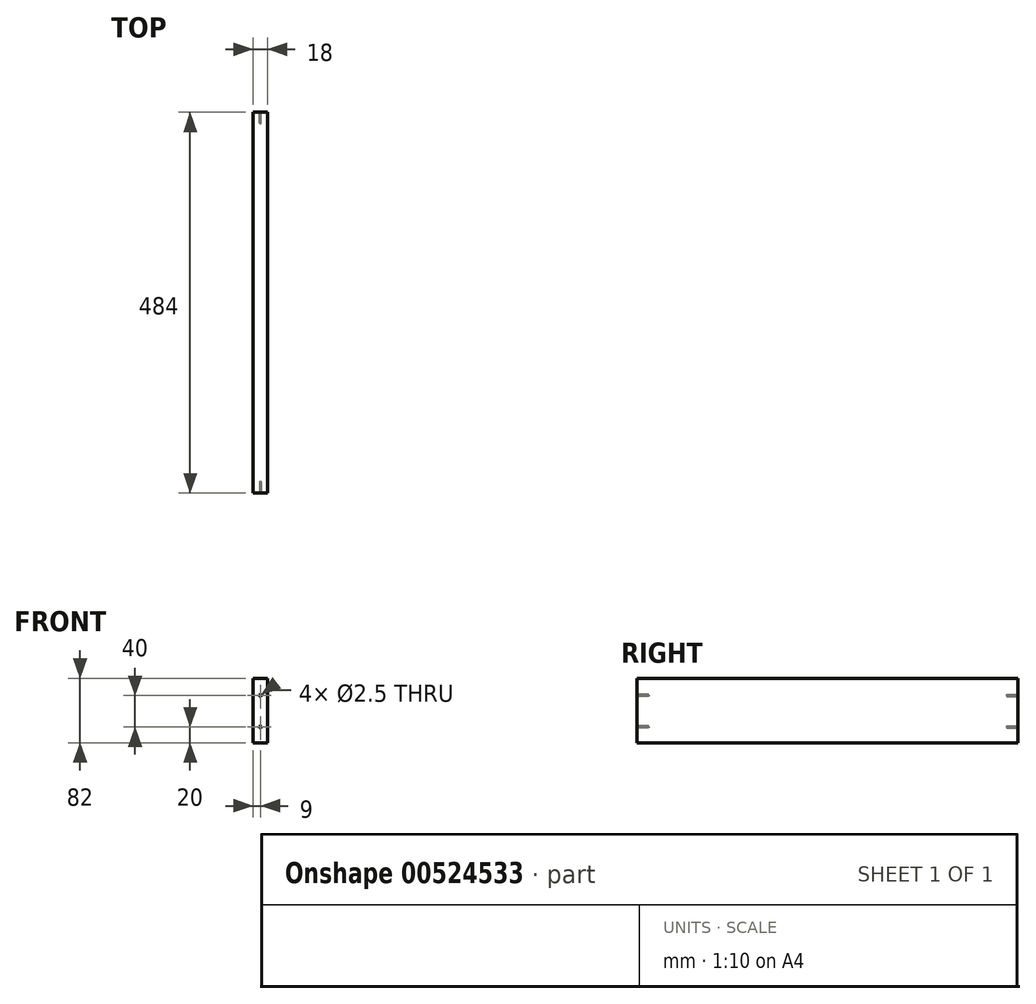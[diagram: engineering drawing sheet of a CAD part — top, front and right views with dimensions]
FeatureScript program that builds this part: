
annotation { "Feature Type Name" : "Feature", "Feature Type Description" : "" }
export const myFeature = defineFeature(function(context is Context, id is Id, definition is map)
    precondition{}
    {
        {
            var Q0;
            Q0=qCreatedBy(makeId("Right.planeOp"),FACE);
            var sketch = newSketch(context, id + "F0", { "sketchPlane" : qUnion([Q0])});
            skLineSegment(sketch, "E0.bottom", {"start": v(0, 0) * mm, "end": v(484, 0) * mm});
            skLineSegment(sketch, "E0.top", {"start": v(0, 82) * mm, "end": v(484, 82) * mm});
            skLineSegment(sketch, "E0.left", {"start": v(0, 0) * mm, "end": v(0, 82) * mm});
            skLineSegment(sketch, "E0.right", {"start": v(484, 0) * mm, "end": v(484, 82) * mm});
            skSolve(sketch);
        }
        {
            var Q0;
            Q0 = qSketchRegion(id + "F0", true);
            extrude(context, id + "F1", {"entities" : qUnion([Q0]), "depth" : 18 * mm, "offsetDistance" : 25 * mm});
        }
        {
            var Q0;
            Q0=makeQuery(id+"F1.opExtrude","SWEPT_FACE",FACE,{"disambiguationData":[OSD([sQuery(id+"F0.wireOp",EDGE,"E0.left")])]});
            var sketch = newSketch(context, id + "F2", { "sketchPlane" : qUnion([Q0])});
            skPoint(sketch, "E1", {"position": v(9, 20) * mm});
            skPoint(sketch, "E2", {"position": v(9, 60) * mm});
            skSolve(sketch);
        }
        {
            var Q0;
            Q0=sQuery(id+"F2.wireOp",VERTEX,"E1");
            var Q1;
            Q1=sQuery(id+"F2.wireOp",VERTEX,"E2");
            var Q2;
            Q2=makeQuery(id+"F1.opExtrude","SWEPT_BODY",BODY,{"disambiguationData":[OSD([sQuery(id+"F0.wireOp",EDGE,"E0.bottom"),sQuery(id+"F0.wireOp",EDGE,"E0.top"),sQuery(id+"F0.wireOp",EDGE,"E0.left"),sQuery(id+"F0.wireOp",EDGE,"E0.right")])]});
            hole(context, id + "F3", {"style" : HoleStyle.SIMPLE, "endStyle" : HoleEndStyle.BLIND, "standardTappedOrClearance" : lookupTablePath({ "standard" : "ISO", "engagement" : "75%", "pitch" : "0.5 mm", "size" : "M3", "type" : "Tapped" }), "standardBlindInLast" : lookupTablePath({ "standard" : "ISO", "engagement" : "75%", "pitch" : "0.5 mm", "size" : "M3", "type" : "Tapped" }), "holeDiameter" : 2.5 * mm, "showTappedDepth" : true, "holeDepth" : 14.5 * mm, "isTappedThrough" : true, "tappedDepth" : 13 * mm, "tapClearance" : 3, "locations" : qUnion([Q0, Q1]), "scope" : qUnion([Q2]), "majorDiameter" : 3 * mm});
        }
        {
            var Q0;
            Q0=makeQuery(id+"F1.opExtrude","SWEPT_FACE",FACE,{"disambiguationData":[OSD([sQuery(id+"F0.wireOp",EDGE,"E0.right")])]});
            var sketch = newSketch(context, id + "F4", { "sketchPlane" : qUnion([Q0])});
            skPoint(sketch, "E3", {"position": v(-9, 20) * mm});
            skPoint(sketch, "E4", {"position": v(-9, 60) * mm});
            skSolve(sketch);
        }
        {
            var Q0;
            Q0=sQuery(id+"F4.wireOp",VERTEX,"E4");
            var Q1;
            Q1=sQuery(id+"F4.wireOp",VERTEX,"E3");
            var Q2;
            Q2=makeQuery(id+"F1.opExtrude","SWEPT_BODY",BODY,{"disambiguationData":[OSD([sQuery(id+"F0.wireOp",EDGE,"E0.bottom"),sQuery(id+"F0.wireOp",EDGE,"E0.top"),sQuery(id+"F0.wireOp",EDGE,"E0.left"),sQuery(id+"F0.wireOp",EDGE,"E0.right")])]});
            hole(context, id + "F5", {"style" : HoleStyle.SIMPLE, "endStyle" : HoleEndStyle.BLIND, "standardTappedOrClearance" : lookupTablePath({ "standard" : "ISO", "engagement" : "75%", "pitch" : "0.5 mm", "size" : "M3", "type" : "Tapped" }), "standardBlindInLast" : lookupTablePath({ "standard" : "ISO", "engagement" : "75%", "pitch" : "0.5 mm", "size" : "M3", "type" : "Tapped" }), "holeDiameter" : 2.5 * mm, "showTappedDepth" : true, "holeDepth" : 14 * mm, "isTappedThrough" : true, "tappedDepth" : 12.5 * mm, "tapClearance" : 3, "locations" : qUnion([Q0, Q1]), "scope" : qUnion([Q2]), "majorDiameter" : 3 * mm});
        }
    });
